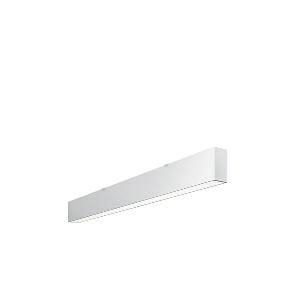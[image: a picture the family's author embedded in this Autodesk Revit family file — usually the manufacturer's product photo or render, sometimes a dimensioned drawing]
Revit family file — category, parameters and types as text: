
# Revit family: dotoo_line_-_dla_2000_830_d_end_00807945_23bb
name_source: partatom
category: Lighting Fixtures
units: mm (PartAtom-declared; Revit-internal decimal feet)

## family parameters
Cut with Voids When Loaded = No
Host = Face
Light Source = No
Part Type = Normal
Room Calculation Point = No
Round Connector Dimension = Use Diameter
Shared = No

## types (1)
- DOTOO.line - DLA 2000/830/D END (1 x LED, 1650 lm, 3000K)
    Apparent Load = 16 VA
    Approval mark = CE
    CIE Flux Codes = 67 91 98 100 100
    Color Rendering = 80-89
    Color Temperature = 3000K
    Control Gear = Electronic ballast
    Default Elevation = 1800 mm
    Description = DLA 2000/830/D|Surface-mounted luminaire.|light source: LED|work equipment: Adjustable electronic ballast, digital DALI|connected load: 220-240 V, 50/60 Hz|Power consumption: approx. 16 W|luminous flux: 1650 lm|luminous efficacy: 103 lm/W|light distribution: Direct|colour temperature: Warm white, ca. 3000 K|class of protection: I|technology: Continuously dimmable|mains lead: Connector|glare control: Prism aperture|special features: DALI Load 1x, TouchDIM - dimming via standard switch, Through-wired, up to 18 m on one mains connection, Flicker-free, Suitable as emergency lighting, Mechanical and electrical connection of the individual modules without tools|
    Frequency = 50 Hz
    Height = 110 mm
    Lamp = 1 x LED
    Lamp Light Flux = 1650 lm
    Lamp count = 1
    Length = 1408 mm
    Luminous efficacy = 103 lm/W
    Manufacturer = Waldmann
    ModVariant = No
    Model = 00807945
    Mounting Place = Ceiling
    Mounting Type = Surface mounted
    Number of Poles = 1
    OnlyDefault = Yes
    Power Factor = 1
    Product Name = DOTOO.line - DLA 2000/830/D END
    Product group = Ceiling mounted luminaire
    ProductGroupID = 3
    Protection Class = Protection class I
    Protection Degree = IP 40
    RLX_Detail_Level = 1
    RLX_Emergency_Light_Flux = 0 lm
    RLX_Emergency_Type = 0
    RLX_Emergency_Type_DB = No
    RlxData = <blob elided: 15237 chars, md5=e8d67ca0>
    Socket = socket
    Standby Power = 0 W
    System Light Flux = 1650 lm
    System Power = 16 W
    Type Comments = Product without accessories
    Type Image = 114350000-00807927.jpg
    URL = http://relux.com
    VarID = ---
    Voltage = 230 V
    Voltage Range = 220-240 V
    Weight = 0.00 kg
    Width = 60 mm  [stored 0.19685 ft]

note: [stored X ft] marks values corroborated as IEEE doubles in the binary element streams (Revit-internal decimal feet)

## geometry (parser evidence)
native form markers: Sweep x12
no freeform markers — native parametric forms only
